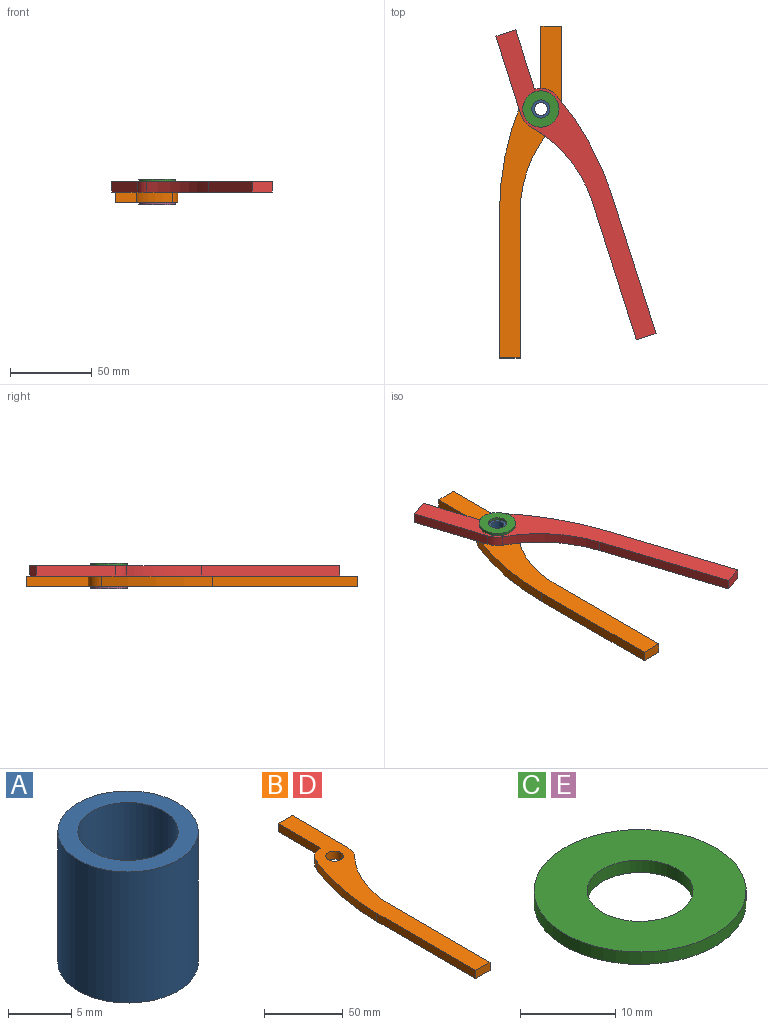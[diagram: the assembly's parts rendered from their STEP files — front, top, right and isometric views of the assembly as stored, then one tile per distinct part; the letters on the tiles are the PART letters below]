
ASSEMBLY  parts=5 mates=4
PART A: 4 faces, bbox 11.1x11.1x12.7 mm
  f0: cylinder r=3.97mm len=12.7mm, axis (0,0,-1), area 316.7mm2, adj f2,f3
  f1: cylinder r=5.56mm len=12.7mm, axis (0,0,-1), area 443.4mm2, adj f2,f3
  f2: plane 11.11x11.11mm, normal (0,0,1), area 47.5mm2, adj f0,f1
  f3: plane 11.11x11.11mm, normal (0,0,-1), area 47.5mm2, adj f0,f1
PART B: 13 faces, bbox 38.1x203.2x6.4 mm
  f0: plane 88.9x6.35mm, normal (1,0,0), area 564.5mm2, adj f1,f9,f11,f12
  f1: cylinder r=79.41mm len=55.09mm, axis (0,0,-1), area 386.6mm2, adj f0,f2,f11,f12
  f2: cylinder r=12.7mm len=8.41mm, axis (0,0,-1), area 58.4mm2, adj f1,f3,f11,f12
  f3: plane 50.8x6.35mm, normal (1,0,0), area 322.6mm2, adj f2,f4,f11,f12
  f4: plane 12.7x6.35mm, normal (0,1,0), area 80.6mm2, adj f3,f5,f11,f12
  f5: plane 38.1x6.35mm, normal (-1,0,0), area 241.9mm2, adj f4,f6,f11,f12
  f6: cylinder r=12.7mm len=11.88mm, axis (0,0,-1), area 97.5mm2, adj f5,f7,f11,f12
  f7: cylinder r=177.71mm len=67.99mm, axis (0,0,-1), area 443mm2, adj f6,f8,f11,f12
  f8: plane 88.9x6.35mm, normal (-1,0,0), area 564.5mm2, adj f7,f9,f11,f12
  f9: plane 12.7x6.35mm, normal (0,-1,0), area 80.6mm2, adj f0,f8,f11,f12
  f10: cylinder r=5.56mm len=11.11mm, axis (0,0,-1), area 221.7mm2, adj f11,f12
  f11: plane 203.2x38.1mm, normal (0,0,1), area 2954.2mm2, adj f0,f1,f2,f3,f4,f5,f6,f7
  f12: plane 203.2x38.1mm, normal (0,0,-1), area 2954.2mm2, adj f0,f1,f2,f3,f4,f5,f6,f7
PART C: 4 faces, bbox 22.2x22.2x1.6 mm
  f0: cylinder r=5.56mm len=11.11mm, axis (0,0,-1), area 55.4mm2, adj f2,f3
  f1: cylinder r=11.11mm len=22.23mm, axis (0,0,-1), area 110.8mm2, adj f2,f3
  f2: plane 22.23x22.23mm, normal (0,0,1), area 291mm2, adj f0,f1
  f3: plane 22.23x22.23mm, normal (0,0,-1), area 291mm2, adj f0,f1
PART D: same geometry as B
PART E: same geometry as C
PLACE A t=(-184.66,185.55,2.02)mm fixed
PLACE B t=(59.24,33.15,2.02)mm
PLACE C rot(axis=(1,0,0),180deg) t=(-192.06,185.55,16.3)mm
PLACE D rot(axis=(0.15,-0.99,0),180deg) t=(-385.19,-35.98,14.72)mm
PLACE E rot(axis=(1,0,0),180deg) t=(-192.06,185.55,2.02)mm
MATE fastened C.f1 <-> A.f0  axis (0,0,-1) through (-192.06,185.55,14.72)mm
MATE revolute D.f2 <-> B.f2  axis (0,0,-1) through (-192.06,185.55,8.37)mm
MATE fastened E.f0 <-> B.f2  axis (0,0,1) through (-192.06,185.55,2.02)mm
MATE fastened A.f0 <-> B.f2  axis (0,0,-1) through (-192.06,185.55,2.02)mm
